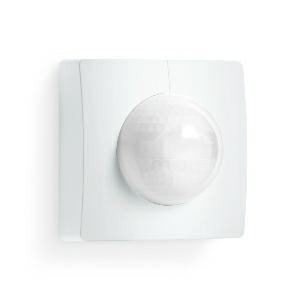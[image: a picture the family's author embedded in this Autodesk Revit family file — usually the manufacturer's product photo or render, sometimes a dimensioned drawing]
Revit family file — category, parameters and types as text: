
# Revit family: is_3180_009113
name_source: partatom
category: Elektroinstallationen
revit_build: Autodesk Revit 2016 (Build: 20190508_0715(x64)
units: mm (PartAtom-declared; Revit-internal decimal feet)

## family parameters
Basisbauteil = Fläche
Beim Laden mit Abzugskörper schneiden = Nein
Bemaßung runder Anschluss = Durchmesser verwenden
Beschriftungsausrichtung beibehalten = Nein
Gemeinsam genutzt = Nein
Raumberechnungspunkt = Nein
Teiletyp = Normal

## types (1)
- IS 3180
    Apparent Load = 0 VA
    Beschreibung = Type: Motion detectors; Dimensions (L x W x H): 65 x 95 x 95 mm; Mains power supply: 220 – 240 V / 50 – 60 Hz; Sensor Technology: passive infrared; Application, place: Outdoors, Indoors; Application, room: corridor / aisle, function room / ancillary room, stairwell, multi-storey / underground car park, outdoors, all round the building, courtyard & driveway, Indoors; Installation site: wall, corner; Installation: Surface wiring; Switching zones: 448 switching zones; Electronic scalability: No; Mechanical scalability: No; Mounting height: 1,80 – 2,50 m; Optimum mounting height: 2 m; Detection angle: 180 °; Angle of aperture: 90 °; Sneak-by guard: Yes; Capability of masking out individual segments: Yes; Reach, radial: r = 3 m (14 m²) / r = 4 m (25 m²); Reach, tangential: r = 6 m (57 m²) / r = 20 m (628 m²); Twilight setting TEACH: Yes; Twilight setting: 2 – 1000 lx; Time setting: 5 sec – 15 min; Switching output 1, resistive: 2000 W; Switching output 1, number of LEDs / fluorescent lamps: 8 pcs.; Constant-lighting control: No; Basic light level function: No; Functions: Normal / test mode, Manual ON / ON-OFF; Settings via: Remote control, Potentiometers, Smart Remote; With remote control: No; Interconnection: Yes; IP-rating: IP54; Material: Plastic; Ambient temperature: -20 – 50 °C; Colour: white; Colour, RAL: 9003; Manufacturer's Warranty: 5 years; Version: COM1 - surface, sq.; PU1, EAN: 4007841009113
    Height = 95 mm
    Hersteller = Steinel
    Length = 65 mm
    Maximum range = 22.153 m
    ModVariant = Nein
    Modell = 009113
    Mounting Type = Surface mounted
    Number of Poles = 1
    OnlyDefault = Ja
    Power Factor = 1
    Product Name = IS 3180
    Product group = Sensor-switched indoor light
    ProductGroupID = 30
    Protection Class = Protection class
    Protection Degree = IP 54
    RlxData = <blob elided: 167269 chars, md5=e846c0e7>
    Sensor characteristics = Semi circular 145°-300°
    Sensor type = Passive (infrared)
    SensorDataFile = <blob elided: 5082 chars, md5=d953030a>
    Type of entry = Motion
    Typenbild = produkt1_009113.jpg
    Typenkommentare = Product without accessories
    URL = http://relux.com
    VarID = ---
    Voltage = 0 V
    Vorgabe-Ansicht = 1800 mm
    Weight = 0.00 kg
    Width = 95 mm

## geometry (parser evidence)
native form markers: Sweep x19
no freeform markers — native parametric forms only
